# Revit family: P300311-012-30
name_source: partatom
category: Lighting Fixtures
revit_build: Autodesk Revit 2014 (Build: 20130308_1515(x64)
units: mm (PartAtom-declared; Revit-internal decimal feet)

## types (1)
- P300311-012-30
    Apparent Load = 13 VA
    Assembly Code = D5020200
    Connector Description = Lighting Connector
    Default Elevation = 48 "
    Description = Pearl LED Collection Two-Light Satin Brass and Opal Glass Modern Style Bath Vanity Wall Light
    Features = Application: Combine elements of simple geometry with the Pearl LED Collection 2-Light Satin Brass Opal Glass LED Modern Bath Vanity Light ideal for any entryway, hallway, foyer, bedroom, sitting room, living room, or bathroom.
Style: Perfect for contemporary and modern style settings.
Finish: A rectangular frame and rounded metal bands combine in an elegant, streamlined design coated in a golden satin brass finish with a reflective polished chrome backplate.
Materials: Constructed from steel to ensure a long product lifespan. Mount the wall light horizontally or vertically.
Glass/Shade: Light sources illuminate opal glass shades that add an extra dimension to the design's modern aesthetic.
Bulbs: For ideal illumination, 2 integrated LED modules are included (13w). 3000K. 90CRI. 812 delivered lumens. Dimmable.
Dimensions: Measures 12-inch length by 5-inch height by 5-1/2-inch depth.
Certifications: cETLus damp location listed, meets California Title 24 JA8-2019.
Pairs With: Pairs with a variety of Progress Lighting fixtures.
Warranty: Our 5-Year Limited Warranty guarantees your complete satisfaction with your purchase and includes professional after-sales customer service support.
    Fixture distribution = Direct
    Glass = Paint - Hubbell - White Texture
    Gold = Hubbell - Gold
    Housing Material = Hubbell - White Glass
    Lamp = LED
    Load Classification = Lighting
    Manufacturer = Progress Lighting
    Model = P300311-012-30
    Power Factor = 1
    Product Documentation Link = https://hubbellcdn.com
    Product Link = https://www.hubbell.com
    URL = https://www.hubbell.com
    Voltage = 120 V
    Warranty = 5 year Warranty
    Wattage Comments = 13W
    Watts = 13 W

## geometry (parser evidence)
native form markers: Sweep x7
no freeform markers — native parametric forms only
